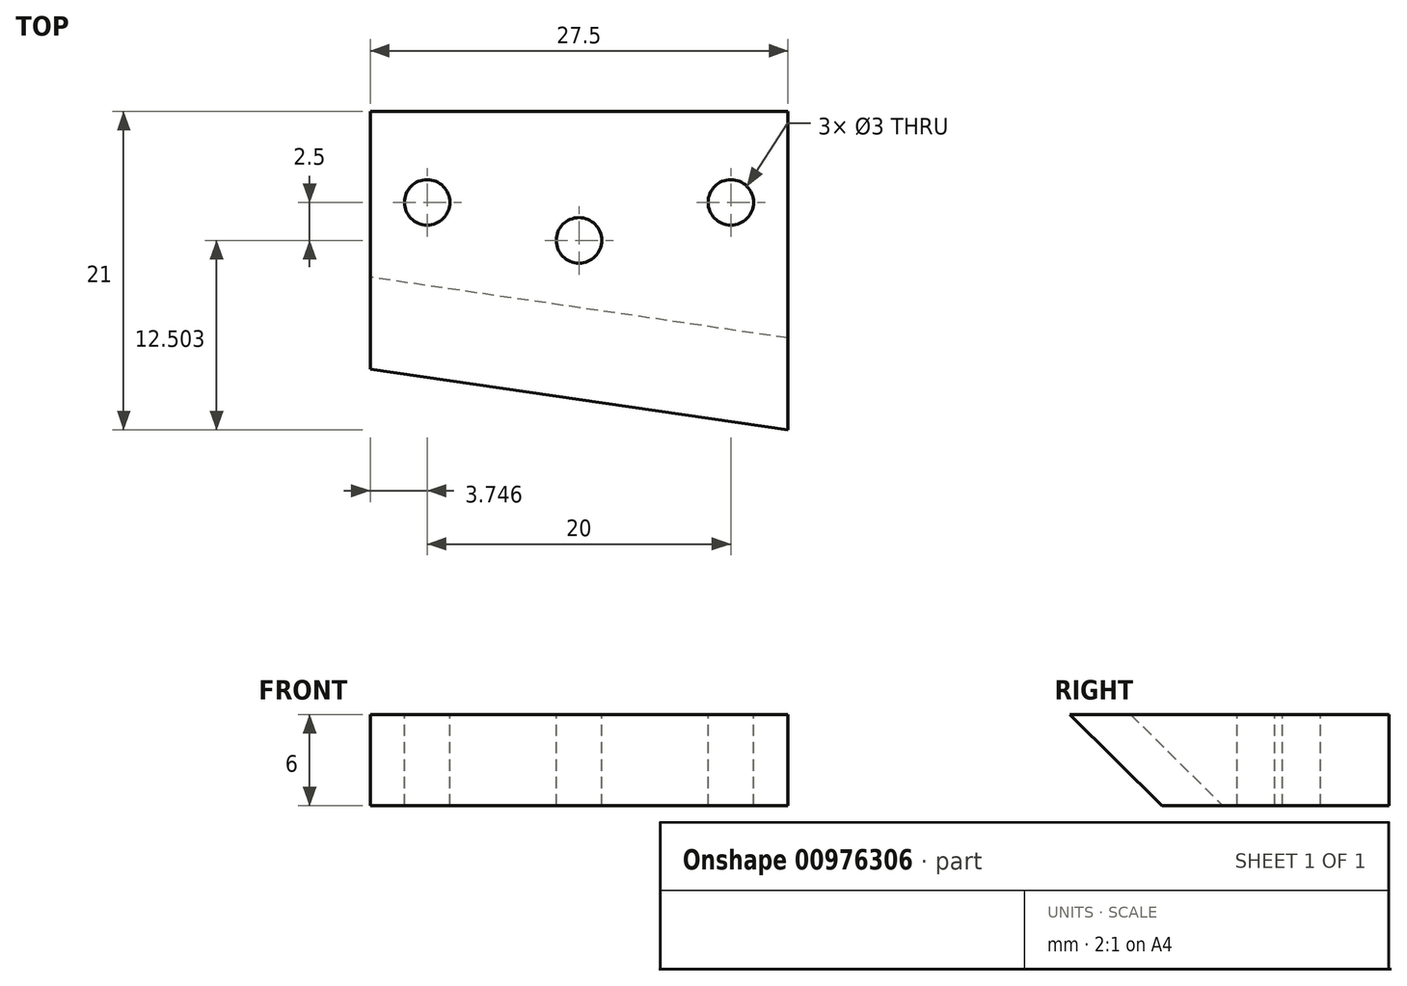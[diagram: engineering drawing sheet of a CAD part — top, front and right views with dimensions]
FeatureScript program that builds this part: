
annotation { "Feature Type Name" : "Feature", "Feature Type Description" : "" }
export const myFeature = defineFeature(function(context is Context, id is Id, definition is map)
    precondition{}
    {
        {
            var Q0;
            Q0=qCreatedBy(makeId("Top.planeOp"),FACE);
            var sketch = newSketch(context, id + "F0", { "sketchPlane" : qUnion([Q0])});
            skLineSegment(sketch, "E0.bottom", {"start": v(-3.73, 6.91) * mm, "end": v(23.77, 6.91) * mm});
            skLineSegment(sketch, "E0.top", {"start": v(-3.73, -14.09) * mm, "end": v(23.77, -14.09) * mm});
            skLineSegment(sketch, "E0.left", {"start": v(-3.73, 6.91) * mm, "end": v(-3.73, -14.09) * mm});
            skLineSegment(sketch, "E0.right", {"start": v(23.77, 6.91) * mm, "end": v(23.77, -14.09) * mm});
            skLineSegment(sketch, "E1", {"start": v(-3.73, -10.09) * mm, "end": v(23.77, -14.09) * mm});
            skSolve(sketch);
        }
        {
            var Q0;
            {var subQ0=sQuery(id+"F0.wireOp",EDGE,"E0.bottom");Q0=makeQuery(id+"F0.imprint","IMPRINT",FACE,{"disambiguationData":[TD([[makeQuery(id+"F0.imprint","IMPRINT",EDGE,{"derivedFrom":subQ0}),-1.0]])]});}
            extrude(context, id + "F1", {"entities" : qUnion([Q0]), "depth" : 6 * mm, "offsetDistance" : 25 * mm});
        }
        {
            var Q0;
            Q0=makeQuery(id+"F1.opExtrude","CAP_EDGE",EDGE,{"disambiguationData":[OSD([sQuery(id+"F0.wireOp",EDGE,"E1")])],"isStart":true});
            chamfer(context, id + "F2", {"entities" : qUnion([Q0]), "width" : 6 * mm, "tangentPropagation" : true});
        }
        {
            var Q0;
            Q0=makeQuery(id+"F1.opExtrude","CAP_FACE",FACE,{"disambiguationData":[OSD([sQuery(id+"F0.wireOp",EDGE,"E0.bottom"),sQuery(id+"F0.wireOp",EDGE,"E0.left"),sQuery(id+"F0.wireOp",EDGE,"E0.right"),sQuery(id+"F0.wireOp",EDGE,"E1")])],"isStart":false});
            var sketch = newSketch(context, id + "F3", { "sketchPlane" : qUnion([Q0])});
            skCircle(sketch, "E2", {"center": v(0.02, 0.91) * mm, "radius": 1.5 * mm});
            skCircle(sketch, "E3", {"center": v(10.02, -1.59) * mm, "radius": 1.5 * mm});
            skCircle(sketch, "E4", {"center": v(20.02, 0.91) * mm, "radius": 1.5 * mm});
            skSolve(sketch);
        }
        {
            var Q0;
            Q0=qSketchRegion(id+"F3",true);
            extrude(context, id + "F4", {"entities" : qUnion([Q0]), "operationType" : NewBodyOperationType.REMOVE, "endBound" : BoundingType.UP_TO_NEXT, "oppositeDirection" : true, "depth" : 25 * mm, "offsetDistance" : 25 * mm});
        }
    });
